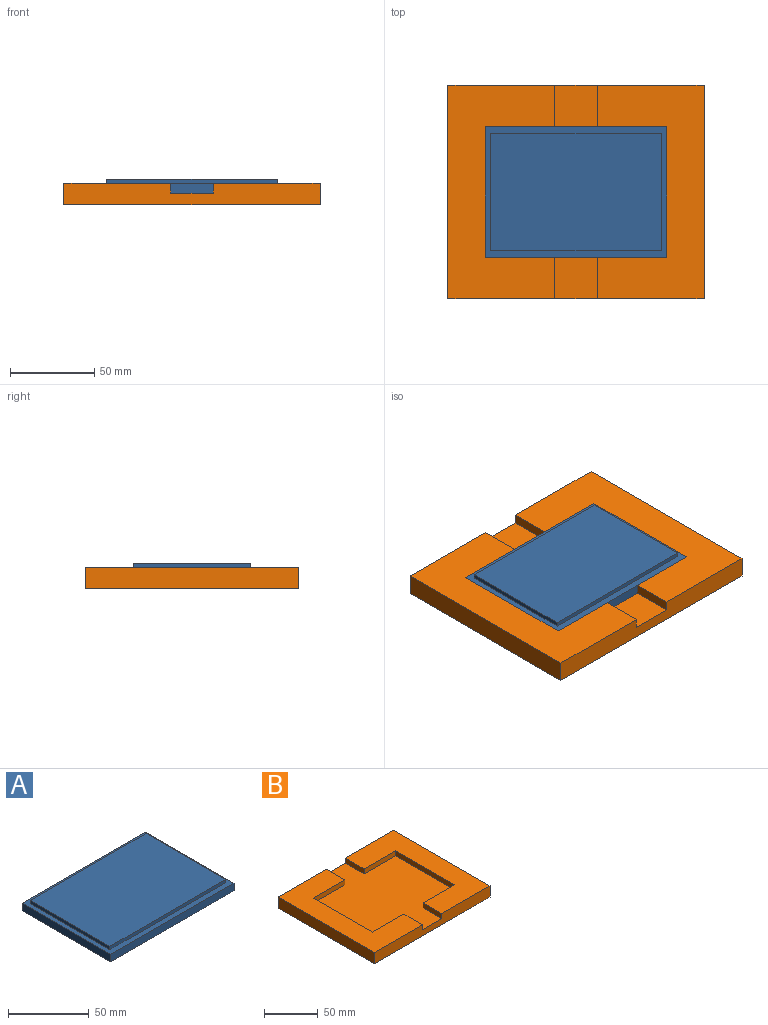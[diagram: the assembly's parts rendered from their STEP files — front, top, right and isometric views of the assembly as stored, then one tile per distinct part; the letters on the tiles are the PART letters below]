
ASSEMBLY  parts=2 mates=1
PART A: 11 faces, bbox 108x77.8x8.3 mm
  f0: plane 107.95x77.79mm, normal (0,0,1), area 1300.4mm2, adj f1,f2,f3,f4,f6,f7,f8,f9
  f1: plane 77.79x5.72mm, normal (1,0,0), area 444.6mm2, adj f0,f2,f4,f5
  f2: plane 107.95x5.72mm, normal (0,1,0), area 616.9mm2, adj f0,f1,f3,f5
  f3: plane 77.79x5.72mm, normal (-1,0,0), area 444.6mm2, adj f0,f2,f4,f5
  f4: plane 107.95x5.72mm, normal (0,-1,0), area 616.9mm2, adj f0,f1,f3,f5
  f5: plane 107.95x77.79mm, normal (0,0,-1), area 8397.2mm2, adj f1,f2,f3,f4
  f6: plane 101.6x2.54mm, normal (0,-1,0), area 258.1mm2, adj f0,f7,f9,f10
  f7: plane 69.85x2.54mm, normal (1,0,0), area 177.4mm2, adj f0,f6,f8,f10
  f8: plane 101.6x2.54mm, normal (0,1,0), area 258.1mm2, adj f0,f7,f9,f10
  f9: plane 69.85x2.54mm, normal (-1,0,0), area 177.4mm2, adj f0,f6,f8,f10
  f10: plane 101.6x69.85mm, normal (0,0,1), area 7096.8mm2, adj f6,f7,f8,f9
PART B: 18 faces, bbox 152.4x127x12.7 mm
  f0: plane 152.4x12.7mm, normal (0,-1,0), area 1790.3mm2, adj f1,f2,f3,f5,f6,f9,f10,f17
  f1: plane 127x63.5mm, normal (0,0,1), area 4853.8mm2, adj f0,f3,f4,f10,f11,f12,f13,f14
  f2: plane 127x63.5mm, normal (0,0,1), area 4853.8mm2, adj f0,f4,f5,f7,f8,f9,f15,f16
  f3: plane 127x12.7mm, normal (1,0,0), area 1612.9mm2, adj f0,f1,f4,f6
  f4: plane 152.4x12.7mm, normal (0,1,0), area 1790.3mm2, adj f1,f2,f3,f5,f6,f14,f15,f17
  f5: plane 127x12.7mm, normal (-1,0,0), area 1612.9mm2, adj f0,f2,f4,f6
  f6: plane 152.4x127mm, normal (0,0,-1), area 19354.8mm2, adj f0,f3,f4,f5
  f7: plane 77.79x5.72mm, normal (1,0,0), area 444.6mm2, adj f2,f8,f16,f17
  f8: plane 41.28x5.72mm, normal (0,1,0), area 235.9mm2, adj f2,f7,f9,f17
  f9: plane 24.61x5.72mm, normal (1,0,0), area 140.6mm2, adj f0,f2,f8,f17
  f10: plane 24.61x5.72mm, normal (-1,0,0), area 140.6mm2, adj f0,f1,f11,f17
  f11: plane 41.28x5.72mm, normal (0,1,0), area 235.9mm2, adj f1,f10,f12,f17
  f12: plane 77.79x5.72mm, normal (-1,0,0), area 444.6mm2, adj f1,f11,f13,f17
  f13: plane 41.28x5.72mm, normal (0,-1,0), area 235.9mm2, adj f1,f12,f14,f17
  f14: plane 24.61x5.72mm, normal (-1,0,0), area 140.6mm2, adj f1,f4,f13,f17
  f15: plane 24.61x5.72mm, normal (1,0,0), area 140.6mm2, adj f2,f4,f16,f17
  f16: plane 41.28x5.72mm, normal (0,-1,0), area 235.9mm2, adj f2,f7,f15,f17
  f17: plane 127x107.95mm, normal (0,0,1), area 9647.2mm2, adj f0,f4,f7,f8,f9,f10,f11,f12
PLACE A t=(0,0,6.98)mm
PLACE B at identity
MATE fastened B.f17 <-> A.f5  axis (0,0,1) through (0,0,6.99)mm
